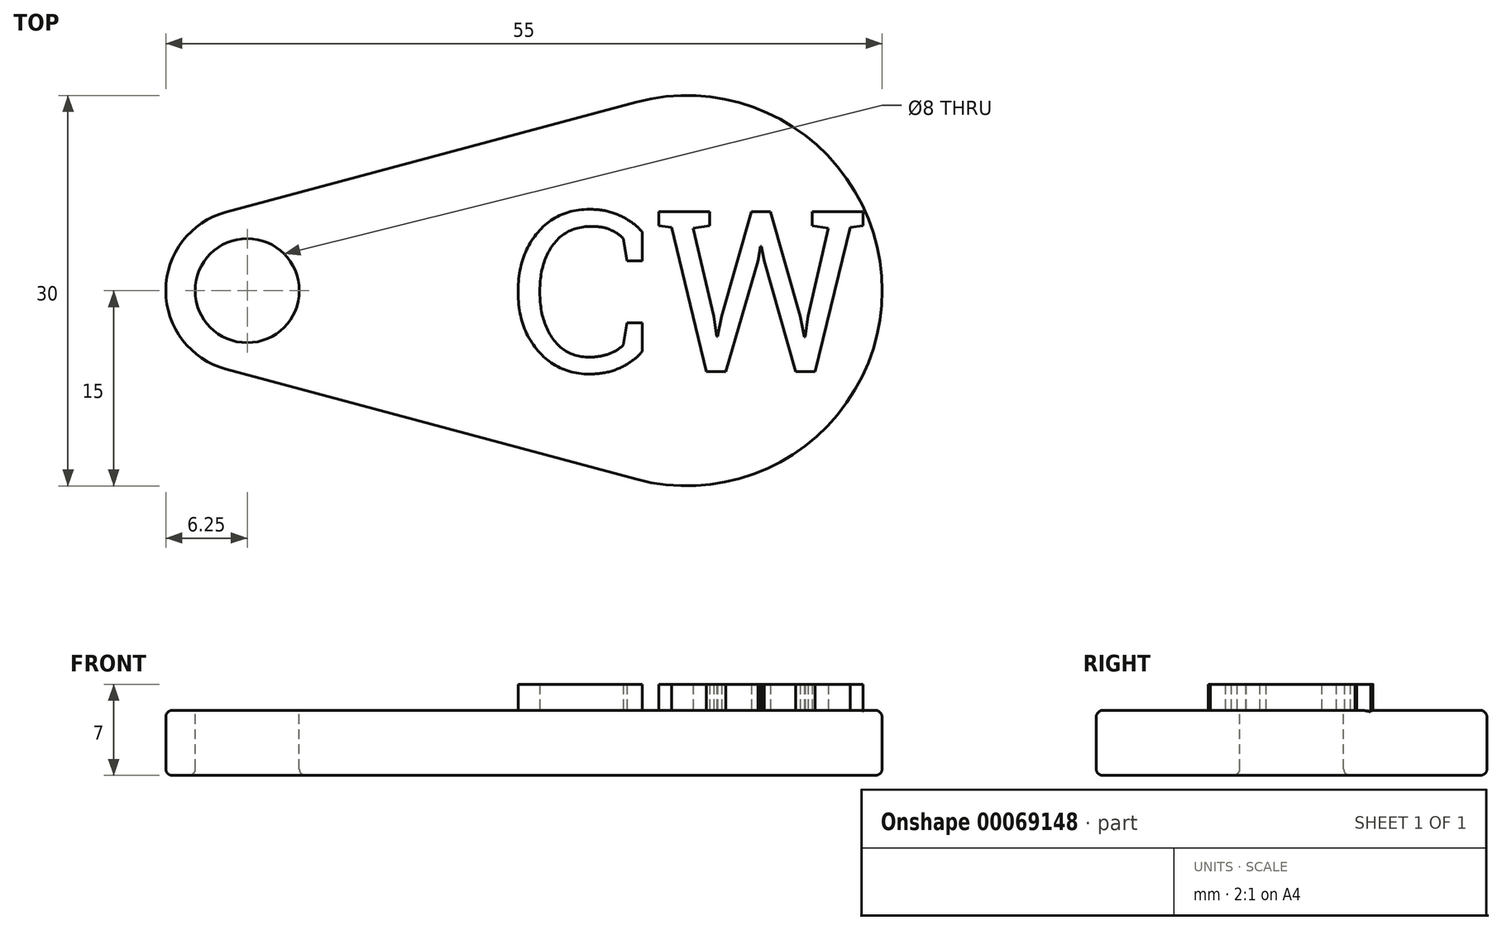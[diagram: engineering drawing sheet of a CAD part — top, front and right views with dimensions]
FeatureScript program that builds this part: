
annotation { "Feature Type Name" : "Feature", "Feature Type Description" : "" }
export const myFeature = defineFeature(function(context is Context, id is Id, definition is map)
    precondition{}
    {
        {
            var Q0;
            Q0=qCreatedBy(makeId("Top.planeOp"),FACE);
            var sketch = newSketch(context, id + "F0", { "sketchPlane" : qUnion([Q0])});
            skCircle(sketch, "E0", {"center": v(-33.75, 0) * mm, "radius": 6.25 * mm});
            skCircle(sketch, "E1", {"center": v(0, 0) * mm, "radius": 15 * mm});
            skLineSegment(sketch, "E2", {"start": v(-35.37, 6.04) * mm, "end": v(-3.89, 14.49) * mm});
            skLineSegment(sketch, "E3", {"start": v(-35.37, -6.04) * mm, "end": v(-3.89, -14.49) * mm});
            skSolve(sketch);
        }
        {
            var Q0;
            {var subQ0=sQuery(id+"F0.wireOp",EDGE,"E0");var subQ1=makeQuery(id+"F0.imprint","INTERSECT",VERTEX,{"derivedFrom":[subQ0,sQuery(id+"F0.wireOp",EDGE,"E2")]});Q0=makeQuery(id+"F0.imprint","IMPRINT",FACE,{"disambiguationData":[TD([[makeQuery(id+"F0.imprint","IMPRINT",EDGE,{"disambiguationData":[TD([[subQ1,-1.0]])],"derivedFrom":subQ0}),1.0]])]});}
            var Q1;
            {var subQ0=sQuery(id+"F0.wireOp",EDGE,"E2");Q1=makeQuery(id+"F0.imprint","IMPRINT",FACE,{"disambiguationData":[TD([[makeQuery(id+"F0.imprint","IMPRINT",EDGE,{"derivedFrom":subQ0}),-1.0]])]});}
            var Q2;
            {var subQ0=sQuery(id+"F0.wireOp",EDGE,"E1");var subQ1=makeQuery(id+"F0.imprint","INTERSECT",VERTEX,{"derivedFrom":[subQ0,sQuery(id+"F0.wireOp",EDGE,"E2")]});Q2=makeQuery(id+"F0.imprint","IMPRINT",FACE,{"disambiguationData":[TD([[makeQuery(id+"F0.imprint","IMPRINT",EDGE,{"disambiguationData":[TD([[subQ1,-1.0]])],"derivedFrom":subQ0}),1.0]])]});}
            extrude(context, id + "F1", {"entities" : qUnion([Q0, Q1, Q2]), "depth" : 5 * mm});
        }
        {
            var Q0;
            Q0=makeQuery(id+"F1.opExtrude","CAP_FACE",FACE,{"disambiguationData":[OSD([sQuery(id+"F0.wireOp",EDGE,"E0"),sQuery(id+"F0.wireOp",EDGE,"E1"),sQuery(id+"F0.wireOp",EDGE,"E2"),sQuery(id+"F0.wireOp",EDGE,"E3")])],"isStart":false});
            var sketch = newSketch(context, id + "F2", { "sketchPlane" : qUnion([Q0])});
            skPoint(sketch, "E4.rect.middle", {"position": v(0, 0) * mm});
            skText(sketch, "E5", { "text": "CW", "fontName": "RobotoSlab-Regular.ttf"});
            const initialGuessF2  = {"E5": [-0.01354, -0.00623, 1, 0, 0.01246]};
            skSetInitialGuess(sketch, initialGuessF2);
            skSolve(sketch);
        }
        {
            var Q0;
            Q0 = qSketchRegion(id + "F2", true);
            extrude(context, id + "F3", {"entities" : qUnion([Q0]), "operationType" : NewBodyOperationType.ADD, "depth" : 2 * mm});
        }
        {
            var Q0;
            Q0=makeQuery(id+"F1.opExtrude","CAP_FACE",FACE,{"disambiguationData":[OSD([sQuery(id+"F0.wireOp",EDGE,"E0"),sQuery(id+"F0.wireOp",EDGE,"E1"),sQuery(id+"F0.wireOp",EDGE,"E2"),sQuery(id+"F0.wireOp",EDGE,"E3")])],"isStart":false});
            var sketch = newSketch(context, id + "F4", { "sketchPlane" : qUnion([Q0])});
            skCircle(sketch, "E6", {"center": v(-33.75, 0) * mm, "radius": 4 * mm});
            skSolve(sketch);
        }
        {
            var Q0;
            Q0=makeQuery(id+"F4.imprint","IMPRINT",FACE,{"disambiguationData":[TD([[makeQuery(id+"F4.imprint","IMPRINT",EDGE,{"derivedFrom":sQuery(id+"F4.wireOp",EDGE,"E6")}),1.0]])]});
            extrude(context, id + "F5", {"entities" : qUnion([Q0]), "operationType" : NewBodyOperationType.REMOVE, "oppositeDirection" : true, "depth" : 25 * mm});
        }
        {
            var Q0;
            Q0=makeQuery(id+"F1.opExtrude","CAP_EDGE",EDGE,{"disambiguationData":[OSD([sQuery(id+"F0.wireOp",EDGE,"E2")])],"isStart":false});
            var Q1;
            Q1=makeQuery(id+"F1.opExtrude","CAP_EDGE",EDGE,{"disambiguationData":[OSD([sQuery(id+"F0.wireOp",EDGE,"E0")])],"isStart":false});
            var Q2;
            Q2=makeQuery(id+"F1.opExtrude","CAP_EDGE",EDGE,{"disambiguationData":[OSD([sQuery(id+"F0.wireOp",EDGE,"E3")])],"isStart":false});
            var Q3;
            Q3=makeQuery(id+"F1.opExtrude","CAP_EDGE",EDGE,{"disambiguationData":[OSD([sQuery(id+"F0.wireOp",EDGE,"E1")])],"isStart":false});
            var Q4;
            Q4=makeQuery(id+"F5.boolean.opBoolean","COPY",EDGE,{"derivedFrom":makeQuery(id+"F5.opExtrude","CAP_EDGE",EDGE,{"disambiguationData":[OSD([sQuery(id+"F4.wireOp",EDGE,"E6")])],"isStart":true})});
            var Q5;
            Q5=makeQuery(id+"F1.opExtrude","CAP_EDGE",EDGE,{"disambiguationData":[OSD([sQuery(id+"F0.wireOp",EDGE,"E2")])],"isStart":true});
            var Q6;
            Q6=makeQuery(id+"F1.opExtrude","CAP_EDGE",EDGE,{"disambiguationData":[OSD([sQuery(id+"F0.wireOp",EDGE,"E0")])],"isStart":true});
            var Q7;
            Q7=makeQuery(id+"F1.opExtrude","CAP_EDGE",EDGE,{"disambiguationData":[OSD([sQuery(id+"F0.wireOp",EDGE,"E3")])],"isStart":true});
            var Q8;
            Q8=makeQuery(id+"F1.opExtrude","CAP_EDGE",EDGE,{"disambiguationData":[OSD([sQuery(id+"F0.wireOp",EDGE,"E1")])],"isStart":true});
            var Q9;
            Q9=makeQuery(id+"F5.boolean.opBoolean","INTERSECT",EDGE,{"derivedFrom":[makeQuery(id+"F1.opExtrude","CAP_FACE",FACE,{"disambiguationData":[OSD([sQuery(id+"F0.wireOp",EDGE,"E0"),sQuery(id+"F0.wireOp",EDGE,"E1"),sQuery(id+"F0.wireOp",EDGE,"E2"),sQuery(id+"F0.wireOp",EDGE,"E3")])],"isStart":true}),makeQuery(id+"F5.opExtrude","SWEPT_FACE",FACE,{"disambiguationData":[OSD([sQuery(id+"F4.wireOp",EDGE,"E6")])]})]});
            fillet(context, id + "F6", {"entities" : qUnion([Q0, Q1, Q2, Q3, Q4, Q5, Q6, Q7, Q8, Q9]), "radius" : 0.5 * mm, "tangentPropagation" : true, "allowEdgeOverflow" : false});
        }
    });
